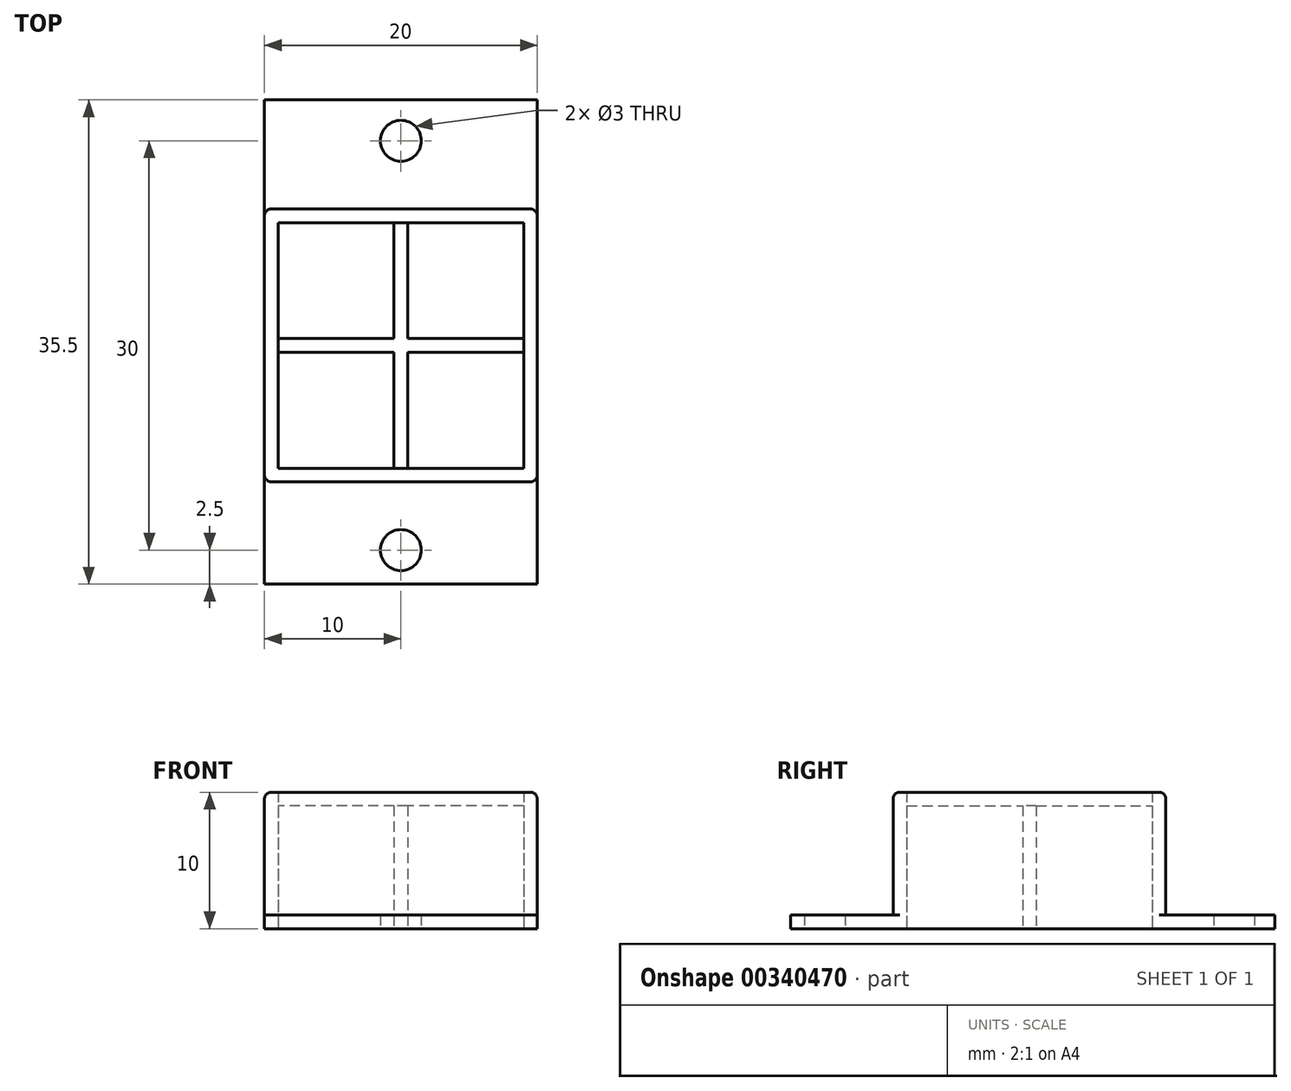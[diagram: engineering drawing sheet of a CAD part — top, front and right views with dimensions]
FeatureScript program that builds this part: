
annotation { "Feature Type Name" : "Feature", "Feature Type Description" : "" }
export const myFeature = defineFeature(function(context is Context, id is Id, definition is map)
    precondition{}
    {
        {
            var Q0;
            Q0=qCreatedBy(makeId("Top.planeOp"),FACE);
            var sketch = newSketch(context, id + "F0", { "sketchPlane" : qUnion([Q0])});
            skPoint(sketch, "E0.middle", {"position": v(0, 0) * mm});
            skLineSegment(sketch, "E1.bottom", {"start": v(10, -10) * mm, "end": v(-10, -10) * mm});
            skLineSegment(sketch, "E1.top", {"start": v(10, 10) * mm, "end": v(-10, 10) * mm});
            skLineSegment(sketch, "E1.left", {"start": v(10, -10) * mm, "end": v(10, 10) * mm});
            skLineSegment(sketch, "E1.right", {"start": v(-10, -10) * mm, "end": v(-10, 10) * mm});
            skSolve(sketch);
        }
        {
            var Q0;
            Q0=makeQuery(id+"F0.imprint","IMPRINT",FACE,{"disambiguationData":[TD([[makeQuery(id+"F0.imprint","IMPRINT",EDGE,{"derivedFrom":sQuery(id+"F0.wireOp",EDGE,"E1.bottom")}),-1.0]])]});
            extrude(context, id + "F1", {"entities" : qUnion([Q0]), "depth" : 10 * mm});
        }
        {
            var Q0;
            Q0=makeQuery(id+"F1.opExtrude","CAP_FACE",FACE,{"disambiguationData":[OSD([sQuery(id+"F0.wireOp",EDGE,"E1.bottom"),sQuery(id+"F0.wireOp",EDGE,"E1.top"),sQuery(id+"F0.wireOp",EDGE,"E1.left"),sQuery(id+"F0.wireOp",EDGE,"E1.right")])],"isStart":true});
            shell(context, id + "F2", {"entities" : qUnion([Q0]), "thickness" : 1 * mm});
        }
        {
            var Q0;
            Q0=qCreatedBy(makeId("Top.planeOp"),FACE);
            var sketch = newSketch(context, id + "F3", { "sketchPlane" : qUnion([Q0])});
            skLineSegment(sketch, "E2.bottom", {"start": v(0.5, -9) * mm, "end": v(-0.5, -9) * mm});
            skLineSegment(sketch, "E2.top", {"start": v(0.5, 9) * mm, "end": v(-0.5, 9) * mm});
            skLineSegment(sketch, "E2.left", {"start": v(0.5, -9) * mm, "end": v(0.5, -0.5) * mm});
            skLineSegment(sketch, "E2.right", {"start": v(-0.5, -9) * mm, "end": v(-0.5, -0.5) * mm});
            skLineSegment(sketch, "E3.bottom", {"start": v(9, 0.5) * mm, "end": v(0.5, 0.5) * mm});
            skLineSegment(sketch, "E3.top", {"start": v(9, -0.5) * mm, "end": v(0.5, -0.5) * mm});
            skLineSegment(sketch, "E3.left", {"start": v(9, 0.5) * mm, "end": v(9, -0.5) * mm});
            skLineSegment(sketch, "E3.right", {"start": v(-9, 0.5) * mm, "end": v(-9, -0.5) * mm});
            skLineSegment(sketch, "E4.trimOffspring", {"start": v(-0.5, 0.5) * mm, "end": v(-0.5, 9) * mm});
            skLineSegment(sketch, "E5.trimOffspring", {"start": v(-0.5, -0.5) * mm, "end": v(-9, -0.5) * mm});
            skLineSegment(sketch, "E6.trimOffspring", {"start": v(0.5, 0.5) * mm, "end": v(0.5, 9) * mm});
            skLineSegment(sketch, "E7.trimOffspring", {"start": v(-0.5, 0.5) * mm, "end": v(-9, 0.5) * mm});
            skSolve(sketch);
        }
        {
            var Q0;
            Q0=qSketchRegion(id+"F3",true);
            extrude(context, id + "F4", {"entities" : qUnion([Q0]), "operationType" : NewBodyOperationType.ADD, "depth" : 9 * mm});
        }
        {
            var Q0;
            Q0=qCreatedBy(makeId("Top.planeOp"),FACE);
            var sketch = newSketch(context, id + "F5", { "sketchPlane" : qUnion([Q0])});
            skLineSegment(sketch, "E8.bottom", {"start": v(-10, -9.5) * mm, "end": v(10, -9.5) * mm});
            skLineSegment(sketch, "E8.top", {"start": v(-10, -17.5) * mm, "end": v(10, -17.5) * mm});
            skLineSegment(sketch, "E8.left", {"start": v(-10, -9.5) * mm, "end": v(-10, -17.5) * mm});
            skLineSegment(sketch, "E8.right", {"start": v(10, -9.5) * mm, "end": v(10, -17.5) * mm});
            skLineSegment(sketch, "E9.bottom", {"start": v(-10, 10) * mm, "end": v(10, 10) * mm});
            skLineSegment(sketch, "E9.top", {"start": v(-10, 18) * mm, "end": v(10, 18) * mm});
            skLineSegment(sketch, "E9.left", {"start": v(-10, 10) * mm, "end": v(-10, 18) * mm});
            skLineSegment(sketch, "E9.right", {"start": v(10, 10) * mm, "end": v(10, 18) * mm});
            skLineSegment(sketch, "E10.bottom", {"start": v(-10, -9.5) * mm, "end": v(-13, -9.5) * mm, "construction": true});
            skLineSegment(sketch, "E10.top", {"start": v(-10, 10) * mm, "end": v(-13, 10) * mm, "construction": true});
            skLineSegment(sketch, "E10.left", {"start": v(-10, -9.5) * mm, "end": v(-10, 10) * mm});
            skLineSegment(sketch, "E10.right", {"start": v(-13, -9.5) * mm, "end": v(-13, 10) * mm, "construction": true});
            skLineSegment(sketch, "E11.bottom", {"start": v(10, -9.5) * mm, "end": v(13, -9.5) * mm, "construction": true});
            skLineSegment(sketch, "E11.top", {"start": v(10, 10) * mm, "end": v(13, 10) * mm, "construction": true});
            skLineSegment(sketch, "E11.left", {"start": v(10, -9.5) * mm, "end": v(10, 10) * mm});
            skLineSegment(sketch, "E11.right", {"start": v(13, -9.5) * mm, "end": v(13, 10) * mm, "construction": true});
            skCircle(sketch, "E12", {"center": v(0, 15) * mm, "radius": 1.5 * mm});
            skCircle(sketch, "E13", {"center": v(0, -15) * mm, "radius": 1.5 * mm});
            skSolve(sketch);
        }
        {
            var Q0;
            Q0=makeQuery(id+"F5.imprint","IMPRINT",FACE,{"disambiguationData":[TD([[makeQuery(id+"F5.imprint","IMPRINT",EDGE,{"derivedFrom":sQuery(id+"F5.wireOp",EDGE,"E10.bottom")}),-1.0]])]});
            var Q1;
            Q1=makeQuery(id+"F5.imprint","IMPRINT",FACE,{"disambiguationData":[TD([[makeQuery(id+"F5.imprint","IMPRINT",EDGE,{"derivedFrom":sQuery(id+"F5.wireOp",EDGE,"E8.bottom")}),-1.0]])]});
            var Q2;
            Q2=makeQuery(id+"F5.imprint","IMPRINT",FACE,{"disambiguationData":[TD([[makeQuery(id+"F5.imprint","IMPRINT",EDGE,{"derivedFrom":sQuery(id+"F5.wireOp",EDGE,"E11.bottom")}),1.0]])]});
            var Q3;
            Q3=makeQuery(id+"F5.imprint","IMPRINT",FACE,{"disambiguationData":[TD([[makeQuery(id+"F5.imprint","IMPRINT",EDGE,{"derivedFrom":sQuery(id+"F5.wireOp",EDGE,"E9.bottom")}),1.0]])]});
            extrude(context, id + "F6", {"entities" : qUnion([Q0, Q1, Q2, Q3]), "operationType" : NewBodyOperationType.ADD, "depth" : 1 * mm});
        }
        {
            var Q0;
            Q0=makeQuery(id+"F1.opExtrude","CAP_FACE",FACE,{"disambiguationData":[OSD([sQuery(id+"F0.wireOp",EDGE,"E1.bottom"),sQuery(id+"F0.wireOp",EDGE,"E1.top"),sQuery(id+"F0.wireOp",EDGE,"E1.left"),sQuery(id+"F0.wireOp",EDGE,"E1.right")])],"isStart":false});
            var sketch = newSketch(context, id + "F7", { "sketchPlane" : qUnion([Q0])});
            skLineSegment(sketch, "E14.bottom", {"start": v(9, 9) * mm, "end": v(-9, 9) * mm});
            skLineSegment(sketch, "E14.top", {"start": v(9, -9) * mm, "end": v(-9, -9) * mm});
            skLineSegment(sketch, "E14.left", {"start": v(9, 9) * mm, "end": v(9, -9) * mm});
            skLineSegment(sketch, "E14.right", {"start": v(-9, 9) * mm, "end": v(-9, -9) * mm});
            skPoint(sketch, "E14.middle", {"position": v(0, 0) * mm});
            skSolve(sketch);
        }
        {
            var Q0;
            Q0=qSketchRegion(id+"F7",true);
            extrude(context, id + "F8", {"entities" : qUnion([Q0]), "operationType" : NewBodyOperationType.REMOVE, "oppositeDirection" : true, "depth" : 1 * mm});
        }
        {
            var Q0;
            Q0=makeQuery(id+"F1.opExtrude","CAP_EDGE",EDGE,{"disambiguationData":[OSD([sQuery(id+"F0.wireOp",EDGE,"E1.bottom")])],"isStart":false});
            var Q1;
            Q1=makeQuery(id+"F1.opExtrude","CAP_EDGE",EDGE,{"disambiguationData":[OSD([sQuery(id+"F0.wireOp",EDGE,"E1.left")])],"isStart":false});
            var Q2;
            Q2=makeQuery(id+"F1.opExtrude","SWEPT_EDGE",EDGE,{"disambiguationData":[OSD([sQuery(id+"F0.wireOp",EDGE,"E1.bottom"),sQuery(id+"F0.wireOp",EDGE,"E1.left")])]});
            var Q3;
            Q3=makeQuery(id+"F1.opExtrude","SWEPT_EDGE",EDGE,{"disambiguationData":[OSD([sQuery(id+"F0.wireOp",EDGE,"E1.bottom"),sQuery(id+"F0.wireOp",EDGE,"E1.right")])]});
            var Q4;
            Q4=makeQuery(id+"F1.opExtrude","CAP_EDGE",EDGE,{"disambiguationData":[OSD([sQuery(id+"F0.wireOp",EDGE,"E1.right")])],"isStart":false});
            var Q5;
            Q5=makeQuery(id+"F1.opExtrude","CAP_EDGE",EDGE,{"disambiguationData":[OSD([sQuery(id+"F0.wireOp",EDGE,"E1.top")])],"isStart":false});
            var Q6;
            Q6=makeQuery(id+"F1.opExtrude","SWEPT_EDGE",EDGE,{"disambiguationData":[OSD([sQuery(id+"F0.wireOp",EDGE,"E1.top"),sQuery(id+"F0.wireOp",EDGE,"E1.left")])]});
            var Q7;
            Q7=makeQuery(id+"F1.opExtrude","SWEPT_EDGE",EDGE,{"disambiguationData":[OSD([sQuery(id+"F0.wireOp",EDGE,"E1.top"),sQuery(id+"F0.wireOp",EDGE,"E1.right")])]});
            fillet(context, id + "F9", {"entities" : qUnion([Q0, Q1, Q2, Q3, Q4, Q5, Q6, Q7]), "radius" : 0.5 * mm, "tangentPropagation" : true, "allowEdgeOverflow" : false});
        }
    });
